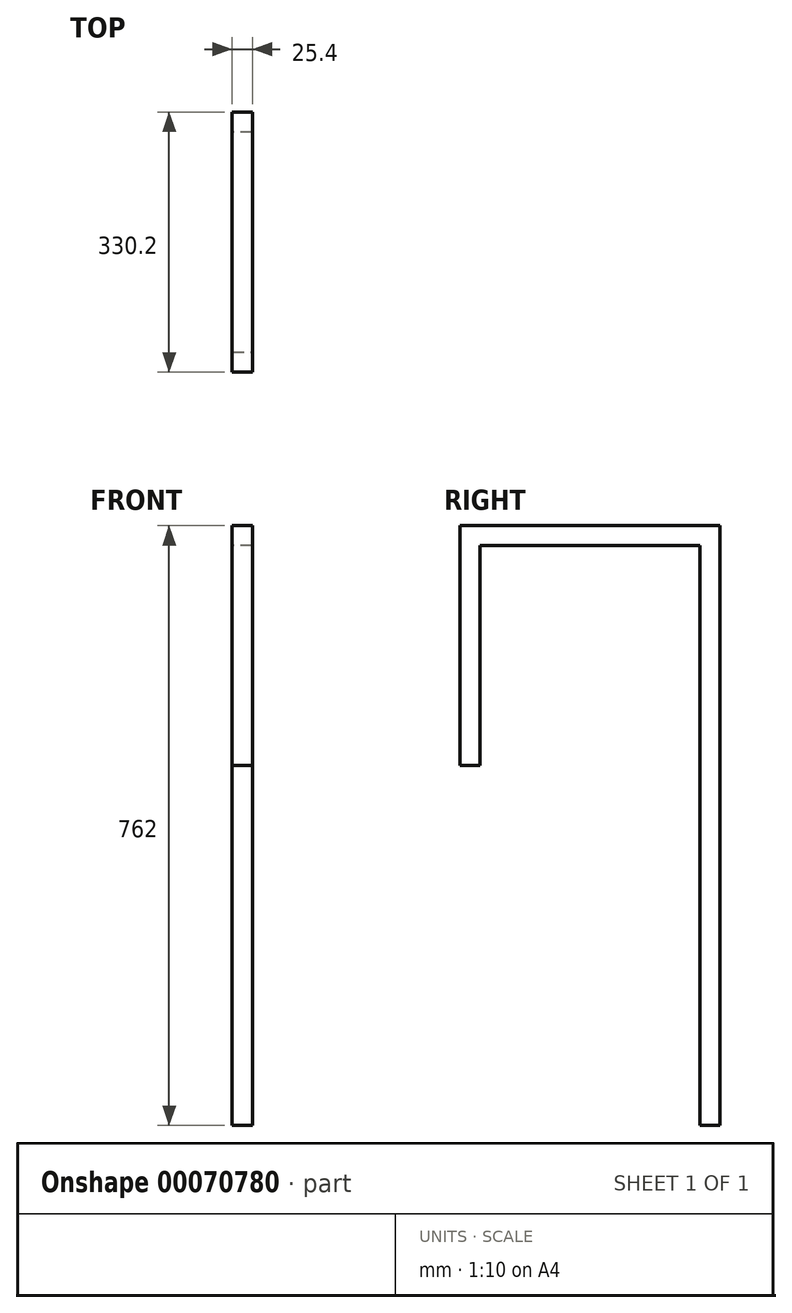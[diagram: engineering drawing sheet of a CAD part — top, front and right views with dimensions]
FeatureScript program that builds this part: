
annotation { "Feature Type Name" : "Feature", "Feature Type Description" : "" }
export const myFeature = defineFeature(function(context is Context, id is Id, definition is map)
    precondition{}
    {
        {
            var Q0;
            Q0=qCreatedBy(makeId("Right.planeOp"),FACE);
            var sketch = newSketch(context, id + "F0", { "sketchPlane" : qUnion([Q0])});
            skLineSegment(sketch, "E0.bottom", {"start": v(-4.87, 460.5) * mm, "end": v(20.53, 460.5) * mm});
            skLineSegment(sketch, "E0.top", {"start": v(-4.87, -301.5) * mm, "end": v(20.53, -301.5) * mm});
            skLineSegment(sketch, "E0.left", {"start": v(-4.87, 460.5) * mm, "end": v(-4.87, -301.5) * mm});
            skLineSegment(sketch, "E0.right", {"start": v(20.53, 460.5) * mm, "end": v(20.53, -301.5) * mm});
            skSolve(sketch);
        }
        {
            var Q0;
            Q0=makeQuery(id+"F0.imprint","IMPRINT",FACE,{"disambiguationData":[TD([[makeQuery(id+"F0.imprint","IMPRINT",EDGE,{"derivedFrom":sQuery(id+"F0.wireOp",EDGE,"E0.bottom")}),-1.0]])]});
            extrude(context, id + "F1", {"entities" : qUnion([Q0]), "depth" : 25.4 * mm});
        }
        {
            var Q0;
            Q0=makeQuery(id+"F1.opExtrude","SWEPT_FACE",FACE,{"disambiguationData":[OSD([sQuery(id+"F0.wireOp",EDGE,"E0.left")])]});
            var sketch = newSketch(context, id + "F2", { "sketchPlane" : qUnion([Q0])});
            skLineSegment(sketch, "E1", {"start": v(0, 460.5) * mm, "end": v(25.4, 460.5) * mm});
            skLineSegment(sketch, "E2", {"start": v(25.4, 460.5) * mm, "end": v(25.4, 435.1) * mm});
            skLineSegment(sketch, "E3", {"start": v(25.4, 435.1) * mm, "end": v(0, 435.1) * mm});
            skLineSegment(sketch, "E4", {"start": v(0, 435.1) * mm, "end": v(0, 460.5) * mm});
            skSolve(sketch);
        }
        {
            var Q0;
            Q0=makeQuery(id+"F2.imprint","IMPRINT",FACE,{"disambiguationData":[TD([[makeQuery(id+"F2.imprint","IMPRINT",EDGE,{"derivedFrom":sQuery(id+"F2.wireOp",EDGE,"E1")}),1.0]])]});
            extrude(context, id + "F3", {"entities" : qUnion([Q0]), "operationType" : NewBodyOperationType.ADD, "depth" : 304.8 * mm});
        }
        {
            var Q0;
            Q0=makeQuery(id+"F3.opExtrude","SWEPT_FACE",FACE,{"disambiguationData":[OSD([sQuery(id+"F2.wireOp",EDGE,"E3")])]});
            var sketch = newSketch(context, id + "F4", { "sketchPlane" : qUnion([Q0])});
            skLineSegment(sketch, "E5", {"start": v(0, 309.67) * mm, "end": v(0, 284.27) * mm});
            skLineSegment(sketch, "E6", {"start": v(0, 284.27) * mm, "end": v(25.4, 284.27) * mm});
            skLineSegment(sketch, "E7", {"start": v(25.4, 284.27) * mm, "end": v(25.4, 309.67) * mm});
            skLineSegment(sketch, "E8", {"start": v(25.4, 309.67) * mm, "end": v(0, 309.67) * mm});
            skSolve(sketch);
        }
        {
            var Q0;
            Q0=makeQuery(id+"F4.imprint","IMPRINT",FACE,{"disambiguationData":[TD([[makeQuery(id+"F4.imprint","IMPRINT",EDGE,{"derivedFrom":sQuery(id+"F4.wireOp",EDGE,"E5")}),1.0]])]});
            extrude(context, id + "F5", {"entities" : qUnion([Q0]), "operationType" : NewBodyOperationType.ADD, "depth" : 279.4 * mm});
        }
    });
